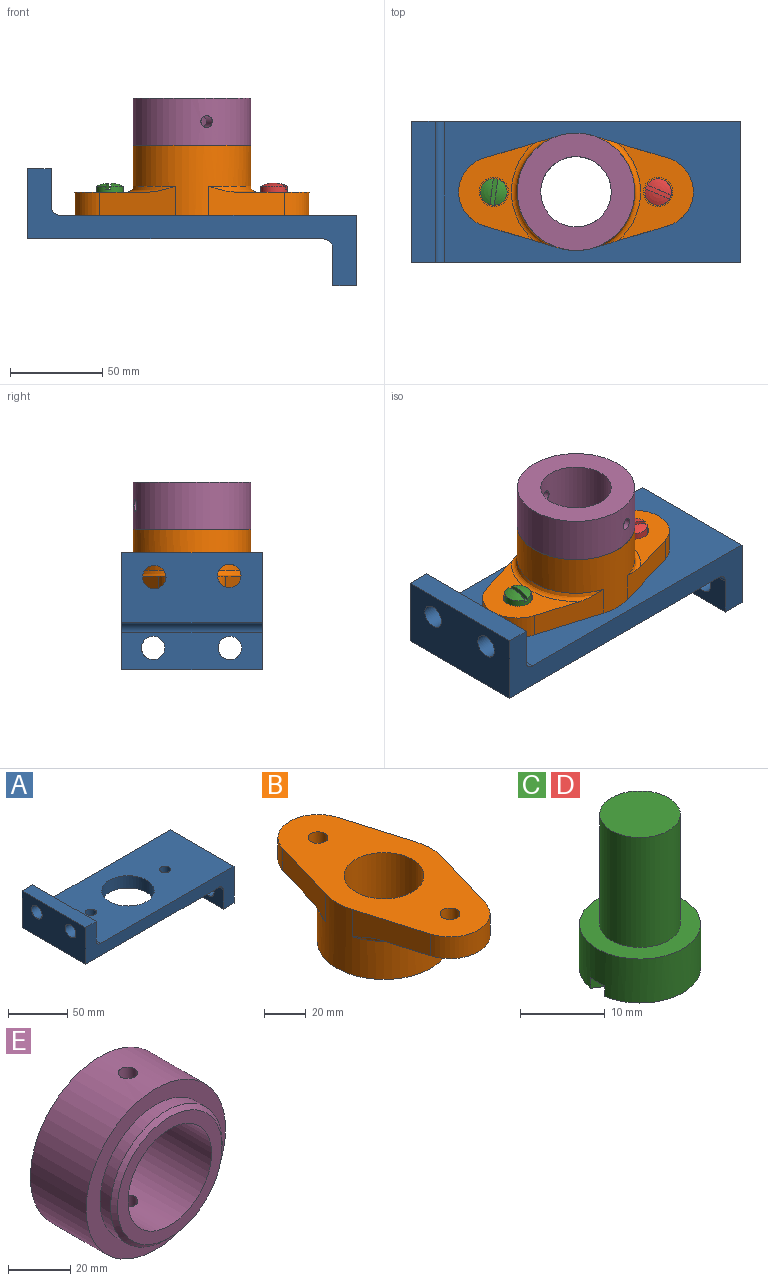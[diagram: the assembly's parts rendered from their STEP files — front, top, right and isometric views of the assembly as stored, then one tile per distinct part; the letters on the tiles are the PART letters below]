
ASSEMBLY  parts=5 mates=5
PART A: 19 faces, bbox 177.8x76.2x63.5 mm
  f0: cylinder r=4.76mm len=12.7mm, axis (0,0,1), area 380mm2, adj f2,f4
  f1: plane 76.2x20.32mm, normal (1,0,0), area 1295mm2, adj f7,f10,f12,f13,f14,f17
  f2: plane 160.02x76.2mm, normal (0,0,1), area 10499.2mm2, adj f0,f5,f6,f7,f8,f10,f17
  f3: plane 76.2x20.32mm, normal (-1,0,0), area 1295mm2, adj f7,f9,f10,f15,f16,f18
  f4: plane 160.02x76.2mm, normal (0,0,-1), area 10499.2mm2, adj f0,f5,f6,f7,f10,f11,f18
  f5: cylinder r=22.23mm len=44.45mm, axis (0,0,1), area 1773.5mm2, adj f2,f4
  f6: cylinder r=4.76mm len=12.7mm, axis (0,0,1), area 380mm2, adj f2,f4
  f7: plane 177.8x63.5mm, normal (0,-1,0), area 2914.3mm2, adj f1,f2,f3,f4,f8,f9,f11,f12
  f8: plane 76.2x38.1mm, normal (1,0,0), area 2649.9mm2, adj f2,f7,f9,f10,f15,f16
  f9: plane 76.2x12.7mm, normal (0,0,-1), area 967.7mm2, adj f3,f7,f8,f10
  f10: plane 177.8x63.5mm, normal (0,1,0), area 2914.3mm2, adj f1,f2,f3,f4,f8,f9,f11,f12
  f11: plane 76.2x38.1mm, normal (-1,0,0), area 2649.9mm2, adj f4,f7,f10,f12,f13,f14
  f12: plane 76.2x12.7mm, normal (0,0,1), area 967.7mm2, adj f1,f7,f10,f11
  f13: cylinder r=6.35mm len=12.7mm, axis (-1,0,0), area 506.7mm2, adj f1,f11
  f14: cylinder r=6.35mm len=12.7mm, axis (-1,0,0), area 506.7mm2, adj f1,f11
  f15: cylinder r=6.35mm len=12.7mm, axis (-1,0,0), area 506.7mm2, adj f3,f8
  f16: cylinder r=6.35mm len=12.7mm, axis (-1,0,0), area 506.7mm2, adj f3,f8
  f17: cylinder r=5.08mm len=76.2mm, axis (0,1,0), area 608mm2, adj f1,f2,f7,f10
  f18: cylinder r=5.08mm len=76.2mm, axis (0,1,0), area 608mm2, adj f3,f4,f7,f10
PART B: 22 faces, bbox 77.1x127x38.1 mm
  f0: plane 52.54x40.49mm, normal (0,0,-1), area 930.5mm2, adj f9,f10,f11,f18,f21
  f1: cylinder r=4.76mm len=9.53mm, axis (0,0,1), area 285mm2, adj f13,f19
  f2: cylinder r=4.76mm len=9.53mm, axis (0,0,1), area 285mm2, adj f13,f16
  f3: plane 63.5x63.5mm, normal (0,0,-1), area 1140.1mm2, adj f12,f14
  f4: cylinder r=19.05mm len=38.1mm, axis (0,0,1), area 3800.3mm2, adj f13,f15
  f5: plane 52.54x40.49mm, normal (0,0,-1), area 930.5mm2, adj f6,f7,f8,f17,f20
  f6: plane 40.82x15.88mm, normal (0.96,0.29,0), area 558.7mm2, adj f5,f7,f12,f13,f20
  f7: cylinder r=19.05mm len=36.51mm, axis (0,0,-1), area 619.9mm2, adj f5,f6,f8,f13
  f8: plane 40.82x15.88mm, normal (-0.96,0.29,0), area 558.7mm2, adj f5,f7,f12,f13,f20
  f9: plane 40.82x15.88mm, normal (-0.96,-0.29,0), area 558.7mm2, adj f0,f10,f12,f13,f21
  f10: cylinder r=19.05mm len=36.51mm, axis (0,0,-1), area 619.9mm2, adj f0,f9,f11,f13
  f11: plane 40.82x15.88mm, normal (0.96,-0.29,0), area 558.7mm2, adj f0,f10,f12,f13,f21
  f12: cylinder r=31.75mm len=63.5mm, axis (0,0,-1), area 5017.9mm2, adj f3,f6,f8,f9,f11,f13,f20,f21
  f13: plane 127x63.5mm, normal (0,0,1), area 4559.2mm2, adj f1,f2,f4,f6,f7,f8,f9,f10
  f14: cylinder r=25.4mm len=50.8mm, axis (0,0,-1), area 1013.4mm2, adj f3,f15
  f15: plane 50.8x50.8mm, normal (0,0,-1), area 886.7mm2, adj f4,f14
  f16: plane 15.88x15.88mm, normal (0,0,-1), area 126.7mm2, adj f2,f17
  f17: cylinder r=7.94mm len=15.88mm, axis (0,0,-1), area 158.3mm2, adj f5,f16
  f18: cylinder r=7.94mm len=15.88mm, axis (0,0,-1), area 158.3mm2, adj f0,f19
  f19: plane 15.88x15.88mm, normal (0,0,-1), area 126.7mm2, adj f1,f18
  f20: torus R=34.92mm, axis (0,0,1), area 343.5mm2, adj f5,f6,f8,f12
  f21: torus R=34.92mm, axis (0,0,1), area 343.5mm2, adj f0,f9,f11,f12
PART C: 9 faces, bbox 14.3x14.3x23.8 mm
  f0: sphere r=16.37mm, area 67mm2, adj f3,f8
  f1: cylinder r=4.76mm len=15.88mm, axis (0,0,1), area 475mm2, adj f2,f4
  f2: plane 9.53x9.53mm, normal (0,0,1), area 71.3mm2, adj f1
  f3: cylinder r=7.15mm len=14.3mm, axis (0,0,1), area 277.7mm2, adj f0,f4,f5,f6,f7,f8
  f4: plane 14.3x14.3mm, normal (0,0,1), area 89.4mm2, adj f1,f3
  f5: sphere r=16.37mm, area 67mm2, adj f3,f7
  f6: plane 14.3x2.39mm, normal (0,0,-1), area 34mm2, adj f3,f7,f8
  f7: plane 14.1x3.18mm, normal (0,-1,0), area 37.4mm2, adj f3,f5,f6
  f8: plane 14.1x3.18mm, normal (0,1,0), area 37.4mm2, adj f0,f3,f6
PART D: same geometry as C
PART E: 9 faces, bbox 63.5x31.8x63.5 mm
  f0: cylinder r=31.75mm len=63.5mm, axis (0,1,0), area 5003.9mm2, adj f3,f5,f7,f8
  f1: plane 47.63x47.63mm, normal (0,-1,0), area 641.3mm2, adj f2,f6
  f2: cylinder r=19.05mm len=38.1mm, axis (0,1,0), area 3737mm2, adj f1,f3,f7,f8
  f3: plane 63.5x63.5mm, normal (0,1,0), area 2026.8mm2, adj f0,f2
  f4: cylinder r=25.4mm len=50.8mm, axis (0,-1,0), area 760.1mm2, adj f5,f6
  f5: plane 63.5x63.5mm, normal (0,-1,0), area 1140.1mm2, adj f0,f4
  f6: cone r=23.81mm half-angle=45deg, axis (0,1,0), area 347.1mm2, adj f1,f4
  f7: cylinder r=3.17mm len=12.97mm, axis (0,0,1), area 254.4mm2, adj f0,f2
  f8: cylinder r=3.17mm len=12.97mm, axis (0,0,1), area 254.4mm2, adj f0,f2
PLACE A at identity fixed
PLACE B rot(axis=(0.71,0.71,0),180deg) t=(-88.9,-38.1,50.8)mm
PLACE C rot(axis=(0.66,-0.75,0),180deg) t=(-177.43,-32.35,50.8)mm
PLACE D rot(axis=(0.98,-0.2,0),180deg) t=(-61.89,-78.99,50.8)mm
PLACE E rot(axis=(0.98,0.13,0.13),90.9deg) t=(-88.9,-38.1,101.6)mm
MATE planar B.f4 <-> A.f5  axis (0,0,-1) through (-88.9,-38.1,38.1)mm
MATE revolute C.f1 <-> B.f1  axis (0,0,-1) through (-133.35,-38.1,47.62)mm
MATE revolute D.f1 <-> B.f2  axis (0,0,-1) through (-44.45,-38.1,47.62)mm
MATE revolute E.f0 <-> B.f4  axis (0,0,1) through (-88.9,-38.1,69.85)mm
MATE fastened A.f0 <-> B.f1  axis (0,0,1) through (-133.35,-38.1,38.1)mm
